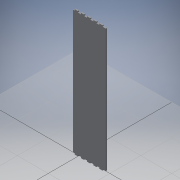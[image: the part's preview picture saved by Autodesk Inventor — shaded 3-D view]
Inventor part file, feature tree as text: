
AUTODESK INVENTOR PART (.ipt)
format: ipt  version: 2019 (Build 230136000, 136)  size: 147,968 bytes
history: native  units: mm
features: reference x23, other x5, extrude x1, sketch x1
ambient origin geometry x8: Origin, YZ Plane, XZ Plane, XY Plane, X Axis, Y Axis, Z Axis, Center Point
bodies: Body1 (feature_tree)
feature tree (30):
  other  "Твердое тело1"
  extrude  "Выдавливание1"  Depth=4.0mm TaperAngle=0.0deg
  sketch  "Эскиз1"
  reference  "Ссылка1"
  reference  "Ссылка2"
  reference  "Ссылка3"
  reference  "Ссылка4"
  reference  "Ссылка5"
  reference  "Ссылка6"
  reference  "Ссылка7"
  reference  "Ссылка8"
  reference  "Ссылка9"
  reference  "Ссылка10"
  reference  "Ссылка11"
  reference  "Ссылка12"
  reference  "Ссылка13"
  reference  "Ссылка14"
  reference  "Ссылка15"
  reference  "Ссылка16"
  reference  "Ссылка17"
  reference  "Ссылка18"
  reference  "Ссылка19"
  reference  "Ссылка20"
  reference  "Ссылка21"
  reference  "Ссылка22"
  reference  "Ссылка23"
  parser-record x1  (decoder bookkeeping rows leaked as tree rows — omitted from the tree; the rows remain in map.json)
  other  "kowsh.iam"
  other  "боковушка:1"
  other  "боковушка:2"
note: 1 file-system path scrubbed to <path> (originals preserved in map.json)
